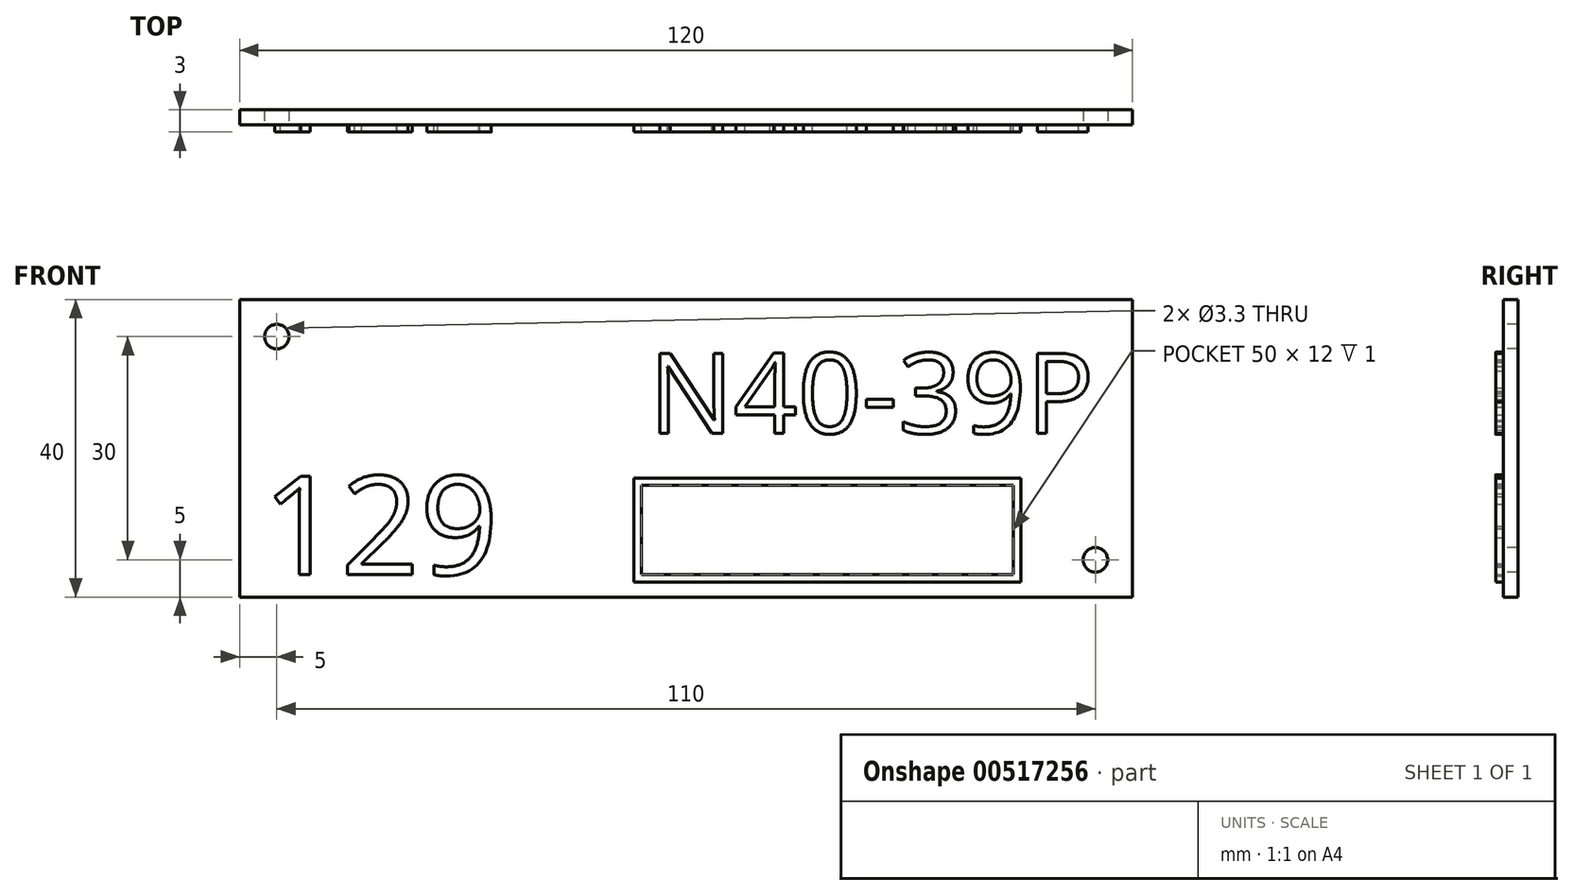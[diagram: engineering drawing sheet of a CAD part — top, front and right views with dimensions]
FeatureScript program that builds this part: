
annotation { "Feature Type Name" : "Feature", "Feature Type Description" : "" }
export const myFeature = defineFeature(function(context is Context, id is Id, definition is map)
    precondition{}
    {
        {
            var Q0;
            Q0=qCreatedBy(makeId("Front.planeOp"),FACE);
            var sketch = newSketch(context, id + "F0", { "sketchPlane" : qUnion([Q0])});
            skLineSegment(sketch, "E0.bottom", {"start": v(60, -20) * mm, "end": v(-60, -20) * mm});
            skLineSegment(sketch, "E0.top", {"start": v(60, 20) * mm, "end": v(-60, 20) * mm});
            skLineSegment(sketch, "E0.left", {"start": v(60, -20) * mm, "end": v(60, 20) * mm});
            skLineSegment(sketch, "E0.right", {"start": v(-60, -20) * mm, "end": v(-60, 20) * mm});
            skPoint(sketch, "E0.middle", {"position": v(0, 0) * mm});
            skSolve(sketch);
        }
        {
            var Q0;
            Q0=makeQuery(id+"F0.imprint","IMPRINT",FACE,{"disambiguationData":[TD([[makeQuery(id+"F0.imprint","IMPRINT",EDGE,{"derivedFrom":sQuery(id+"F0.wireOp",EDGE,"E0.bottom")}),-1.0]])]});
            extrude(context, id + "F1", {"entities" : qUnion([Q0]), "depth" : 2 * mm});
        }
        {
            var Q0;
            Q0=makeQuery(id+"F1.opExtrude","CAP_FACE",FACE,{"disambiguationData":[OSD([sQuery(id+"F0.wireOp",EDGE,"E0.bottom"),sQuery(id+"F0.wireOp",EDGE,"E0.top"),sQuery(id+"F0.wireOp",EDGE,"E0.left"),sQuery(id+"F0.wireOp",EDGE,"E0.right")])],"isStart":false});
            var sketch = newSketch(context, id + "F2", { "sketchPlane" : qUnion([Q0])});
            skPoint(sketch, "E1", {"position": v(-55, 15) * mm});
            skPoint(sketch, "E2", {"position": v(55, -15) * mm});
            skSolve(sketch);
        }
        {
            var Q0;
            Q0=sQuery(id+"F2.wireOp",VERTEX,"E1");
            var Q1;
            Q1=sQuery(id+"F2.wireOp",VERTEX,"E2");
            var Q2;
            Q2=makeQuery(id+"F1.opExtrude","SWEPT_BODY",BODY,{"disambiguationData":[OSD([sQuery(id+"F0.wireOp",EDGE,"E0.bottom"),sQuery(id+"F0.wireOp",EDGE,"E0.top"),sQuery(id+"F0.wireOp",EDGE,"E0.left"),sQuery(id+"F0.wireOp",EDGE,"E0.right")])]});
            hole(context, id + "F3", {"style" : HoleStyle.SIMPLE, "endStyle" : HoleEndStyle.THROUGH, "holeDiameter" : 3.3 * mm, "locations" : qUnion([Q0, Q1]), "scope" : qUnion([Q2]), "isTappedThrough" : true});
        }
        {
            var Q0;
            Q0=makeQuery(id+"F1.opExtrude","CAP_FACE",FACE,{"disambiguationData":[OSD([sQuery(id+"F0.wireOp",EDGE,"E0.bottom"),sQuery(id+"F0.wireOp",EDGE,"E0.top"),sQuery(id+"F0.wireOp",EDGE,"E0.left"),sQuery(id+"F0.wireOp",EDGE,"E0.right")])],"isStart":false});
            var sketch = newSketch(context, id + "F4", { "sketchPlane" : qUnion([Q0])});
            skText(sketch, "E3", { "text": "N40-39P", "fontName": "OpenSans-Regular.ttf"});
            const initialGuessF4  = {"E3": [-0.005, 0.002, 1, 0, 0.01086]};
            skSetInitialGuess(sketch, initialGuessF4);
            skSolve(sketch);
        }
        {
            var Q0;
            Q0=qSketchRegion(id+"F4",true);
            extrude(context, id + "F5", {"entities" : qUnion([Q0]), "operationType" : NewBodyOperationType.ADD, "depth" : 1 * mm});
        }
        {
            var Q0;
            {var subQ0=sQuery(id+"F0.wireOp",EDGE,"E0.top");var subQ1=sQuery(id+"F0.wireOp",EDGE,"E0.left");var subQ2=sQuery(id+"F0.wireOp",EDGE,"E0.right");var subQ3=sQuery(id+"F0.wireOp",EDGE,"E0.bottom");Q0=makeQuery(id+"F5.boolean.opBoolean","SPLIT",FACE,{"disambiguationData":[TD([makeQuery(id+"F1.opExtrude","SWEPT_FACE",FACE,{"disambiguationData":[OSD([subQ3])]})])],"derivedFrom":makeQuery(id+"F1.opExtrude","CAP_FACE",FACE,{"disambiguationData":[OSD([subQ3,subQ0,subQ1,subQ2])],"isStart":false})});}
            var sketch = newSketch(context, id + "F6", { "sketchPlane" : qUnion([Q0])});
            skText(sketch, "E4", { "text": "129", "fontName": "OpenSans-Regular.ttf"});
            const initialGuessF6  = {"E4": [-0.057, -0.017, 1, 0, 0.01335]};
            skSetInitialGuess(sketch, initialGuessF6);
            skSolve(sketch);
        }
        {
            var Q0;
            Q0=qSketchRegion(id+"F6",true);
            extrude(context, id + "F7", {"entities" : qUnion([Q0]), "operationType" : NewBodyOperationType.ADD, "depth" : 1 * mm});
        }
        {
            var Q0;
            {var subQ46=sQuery(id+"F0.wireOp",EDGE,"E0.top");var subQ48=sQuery(id+"F0.wireOp",EDGE,"E0.left");var subQ66=sQuery(id+"F0.wireOp",EDGE,"E0.right");var subQ76=sQuery(id+"F0.wireOp",EDGE,"E0.bottom");var subQ77=makeQuery(id+"F1.opExtrude","SWEPT_FACE",FACE,{"disambiguationData":[OSD([subQ76])]});Q0=makeQuery(id+"F7.boolean.opBoolean","SPLIT",FACE,{"disambiguationData":[TD([subQ77])],"derivedFrom":makeQuery(id+"F5.boolean.opBoolean","SPLIT",FACE,{"disambiguationData":[TD([subQ77])],"derivedFrom":makeQuery(id+"F1.opExtrude","CAP_FACE",FACE,{"disambiguationData":[OSD([subQ76,subQ46,subQ48,subQ66])],"isStart":false})})});}
            var sketch = newSketch(context, id + "F8", { "sketchPlane" : qUnion([Q0])});
            skLineSegment(sketch, "E5.bottom", {"start": v(45, -18) * mm, "end": v(-7, -18) * mm});
            skLineSegment(sketch, "E5.top", {"start": v(45, -4) * mm, "end": v(-7, -4) * mm});
            skLineSegment(sketch, "E5.left", {"start": v(45, -18) * mm, "end": v(45, -4) * mm});
            skLineSegment(sketch, "E5.right", {"start": v(-7, -18) * mm, "end": v(-7, -4) * mm});
            skPoint(sketch, "E5.middle", {"position": v(19, -11) * mm});
            skLineSegment(sketch, "E6.0", {"start": v(44, -5) * mm, "end": v(-6, -5) * mm});
            skLineSegment(sketch, "E6.1", {"start": v(44, -17) * mm, "end": v(44, -5) * mm});
            skLineSegment(sketch, "E6.2", {"start": v(44, -17) * mm, "end": v(-6, -17) * mm});
            skLineSegment(sketch, "E6.3", {"start": v(-6, -17) * mm, "end": v(-6, -5) * mm});
            skSolve(sketch);
        }
        {
            var Q0;
            Q0=makeQuery(id+"F8.imprint","IMPRINT",FACE,{"disambiguationData":[TD([[makeQuery(id+"F8.imprint","IMPRINT",EDGE,{"derivedFrom":sQuery(id+"F8.wireOp",EDGE,"E5.bottom")}),-1.0]])]});
            extrude(context, id + "F9", {"entities" : qUnion([Q0]), "operationType" : NewBodyOperationType.ADD, "depth" : 1 * mm});
        }
    });
